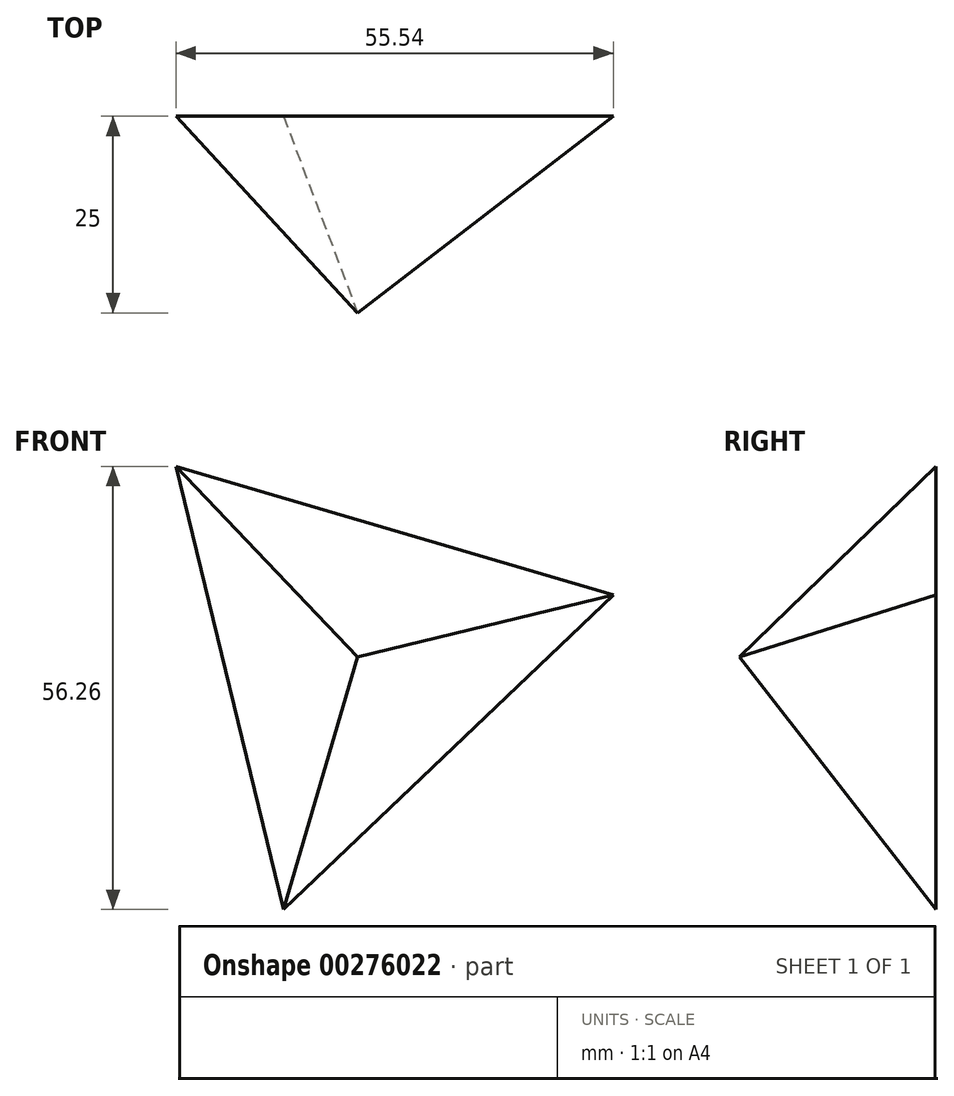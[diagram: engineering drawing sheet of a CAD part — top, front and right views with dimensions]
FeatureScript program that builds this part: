
annotation { "Feature Type Name" : "Feature", "Feature Type Description" : "" }
export const myFeature = defineFeature(function(context is Context, id is Id, definition is map)
    precondition{}
    {
        {
            var Q0;
            Q0=qCreatedBy(makeId("Front.planeOp"),FACE);
            var sketch = newSketch(context, id + "F0", { "sketchPlane" : qUnion([Q0])});
            skCircle(sketch, "E0.cCircle", {"center": v(0, 0) * mm, "radius": 33.42 * mm, "construction": true});
            skLineSegment(sketch, "E0.0", {"start": v(-23.06, 24.2) * mm, "end": v(32.48, 7.87) * mm});
            skLineSegment(sketch, "E0.1", {"start": v(32.48, 7.87) * mm, "end": v(-9.42, -32.07) * mm});
            skLineSegment(sketch, "E0.2", {"start": v(-9.42, -32.07) * mm, "end": v(-23.06, 24.2) * mm});
            skSolve(sketch);
        }
        {
            var Q0;
            Q0=qCreatedBy(makeId("Front.planeOp"),FACE);
            cPlane(context, id + "F1", {"entities" : qUnion([Q0]), "cplaneType" : CPlaneType.OFFSET, "offset" : 25 * mm, "width" : 150 * mm, "height" : 150 * mm});
        }
        {
            var Q0;
            Q0=qCreatedBy(id+"F1.planeOp",FACE);
            var sketch = newSketch(context, id + "F2", { "sketchPlane" : qUnion([Q0])});
            skPoint(sketch, "E1", {"position": v(0, 0) * mm});
            skSolve(sketch);
        }
        {
            var Q0;
            Q0=makeQuery(id+"F0.imprint","IMPRINT",FACE,{"disambiguationData":[TD([[makeQuery(id+"F0.imprint","IMPRINT",EDGE,{"derivedFrom":sQuery(id+"F0.wireOp",EDGE,"E0.0")}),-1.0]])]});
            var Q1;
            Q1=sQuery(id+"F2.wireOp",VERTEX,"E1");
            loft(context, id + "F3", {"sheetProfilesArray" : [{ "sheetProfileEntities" : qUnion([Q0]) }, { "sheetProfileEntities" : qUnion([Q1]) }]});
        }
    });
